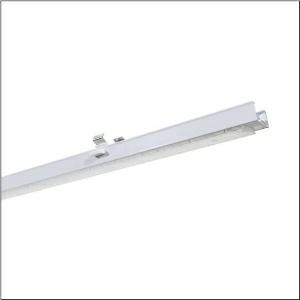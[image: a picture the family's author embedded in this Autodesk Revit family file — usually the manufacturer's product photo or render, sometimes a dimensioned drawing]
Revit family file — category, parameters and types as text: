
# Revit family: trunking_flex_31_51re11ma46b
name_source: partatom
category: Lighting Fixtures
units: mm (PartAtom-declared; Revit-internal decimal feet)

## family parameters
Cut with Voids When Loaded = No
Host = Face
Light Source = No
Part Type = Normal
Room Calculation Point = No
Round Connector Dimension = Use Diameter
Shared = No

## types (1)
- --- (1 x LED, 6400 lm, 40 W, 4000K)
    Apparent Load = 40 VA
    CIE Flux Codes = 83 93 98 100 100
    Color Rendering = 80
    Color Temperature = 4000K
    Default Elevation = 1800 mm
    Description = Trunking Flex 31, luminaire insert, of extruded aluminium section, coated, traffic white (RAL 9016), length: 1.172mm, width: 91mm, height: 53mm, LED rated luminous flux: 6.400lm, light colour: 840, control gear: ON/OFF Multilumen, with system connector: socket, mains connection: 220..240V, AC, 50/60Hz, rated input power: 40W, luminous flux adjustable on luminaire in four steps (3420/4540/5580/6630lm), connected load according to luminous flux setting (20/26/33/40W), primary light control with lens, of plastic, primary optical cover: cover, of PMMA, light emission: direct distribution, protection rating (complete): IP20, insulation class (complete): insulation class I (protective earthing), certification: CE, UKCA, impact resistance: IK02, permissible ambient temperature for indoor applications: -20..+40°C, packaging unit: 1 piece
    Height = 58 mm
    Lamp = 1 x LED
    Lamp Light Flux = 6400 lm
    Lamp Power = 40 W
    Lamp count = 1
    Length = 1172 mm
    Luminous efficacy = 160 lm/W
    Manufacturer = Siteco
    ModVariant = No
    Model = 51RE11MA46B
    Mounting Place = Ceiling
    Mounting Type = Pendant
    Number of Poles = 1
    OnlyDefault = Yes
    Power Factor = 1
    Product Name = Trunking Flex 31
    Product group = luminaire insert
    ProductGroupID = 902
    Protection Class = Protection class I
    Protection Degree = IP 20
    RLX_Detail_Level = 1
    RLX_Emergency_Light_Flux = 0 lm
    RLX_Emergency_Type = 0
    RLX_Emergency_Type_DB = No
    RlxData = <blob elided: 19877 chars, md5=3a2e4f43>
    Socket = socket
    Standby Power = 0 W
    System Light Flux = 6400 lm
    System Power = 40 W
    Type Comments = factory setting: luminous flux: 100 % | (ON | ON) | 300 mA
    Type Image = l_1266702.jpg
    URL = http://relux.com
    VarID = @adj_059282
    Voltage = 0 V
    Weight = 0.00 kg
    Width = 65 mm

## geometry (parser evidence)
native form markers: Blend x4, Sweep x10
no freeform markers — native parametric forms only
